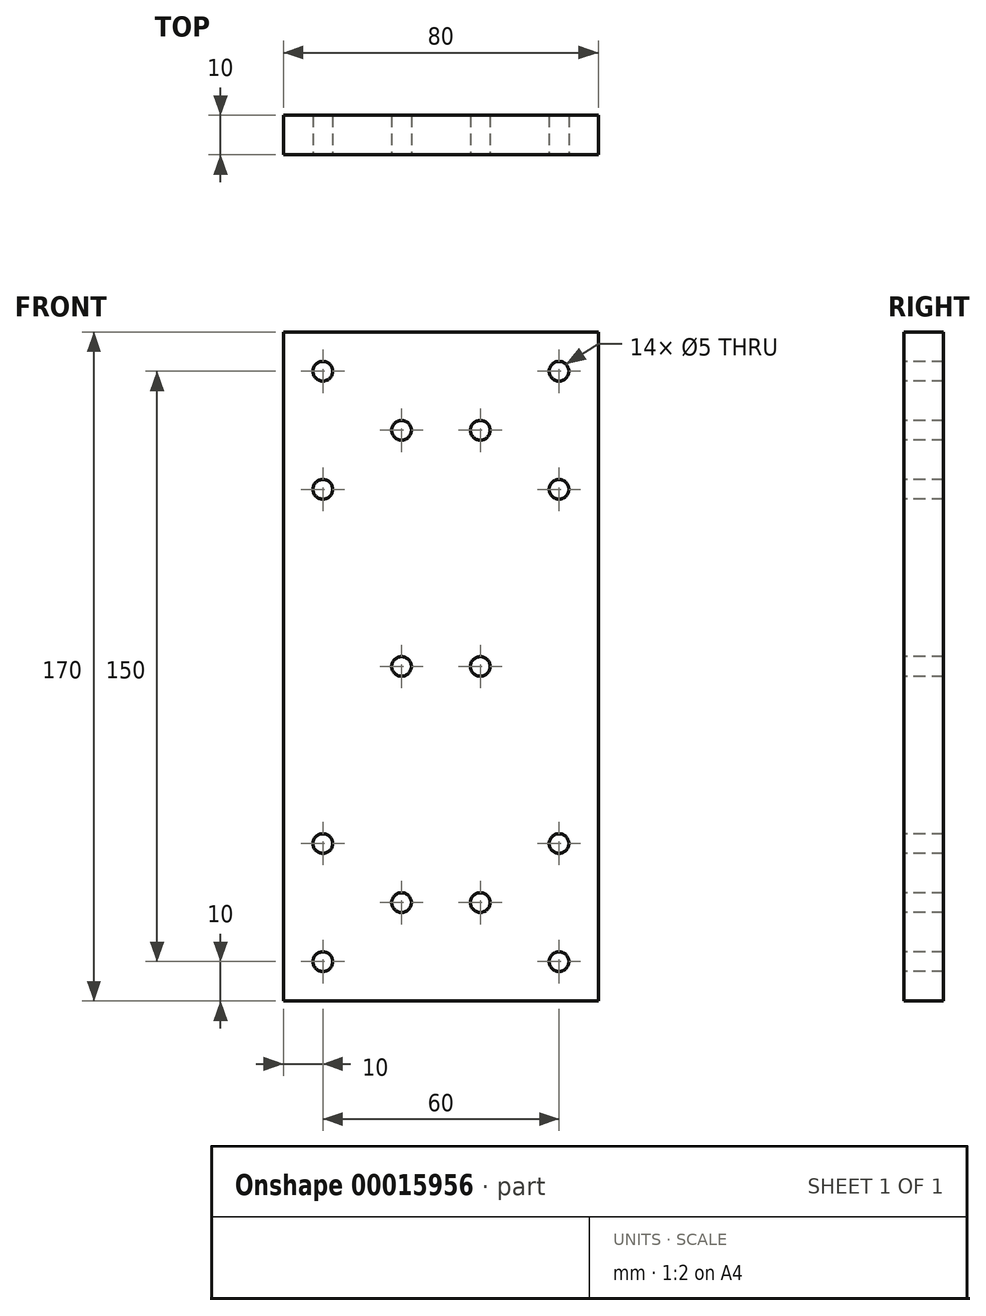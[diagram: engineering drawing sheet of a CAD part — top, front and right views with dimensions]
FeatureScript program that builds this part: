
annotation { "Feature Type Name" : "Feature", "Feature Type Description" : "" }
export const myFeature = defineFeature(function(context is Context, id is Id, definition is map)
    precondition{}
    {
        {
            var Q0;
            Q0=qCreatedBy(makeId("Front.planeOp"),FACE);
            var sketch = newSketch(context, id + "F0", { "sketchPlane" : qUnion([Q0])});
            skLineSegment(sketch, "E0.bottom", {"start": v(0, 0) * mm, "end": v(80, 0) * mm});
            skLineSegment(sketch, "E0.top", {"start": v(0, 170) * mm, "end": v(80, 170) * mm});
            skLineSegment(sketch, "E0.left", {"start": v(0, 0) * mm, "end": v(0, 170) * mm});
            skLineSegment(sketch, "E0.right", {"start": v(80, 0) * mm, "end": v(80, 170) * mm});
            skSolve(sketch);
        }
        {
            var Q0;
            Q0 = qSketchRegion(id + "F0", true);
            extrude(context, id + "F1", {"entities" : qUnion([Q0]), "oppositeDirection" : true, "depth" : 10 * mm});
        }
        {
            var Q0;
            Q0=makeQuery(id+"F1.opExtrude","CAP_FACE",FACE,{"disambiguationData":[OSD([sQuery(id+"F0.wireOp",EDGE,"E0.bottom"),sQuery(id+"F0.wireOp",EDGE,"E0.top"),sQuery(id+"F0.wireOp",EDGE,"E0.left"),sQuery(id+"F0.wireOp",EDGE,"E0.right")])],"isStart":true});
            var sketch = newSketch(context, id + "F2", { "sketchPlane" : qUnion([Q0])});
            skLineSegment(sketch, "E1.0", {"start": v(0, 160) * mm, "end": v(80, 160) * mm, "construction": true});
            skLineSegment(sketch, "E2.0", {"start": v(10, 0) * mm, "end": v(10, 170) * mm, "construction": true});
            skLineSegment(sketch, "E3.0", {"start": v(0, 10) * mm, "end": v(80, 10) * mm, "construction": true});
            skLineSegment(sketch, "E4", {"start": v(40, 170) * mm, "end": v(40, 0) * mm, "construction": true});
            skLineSegment(sketch, "E5", {"start": v(80, 85) * mm, "end": v(0, 85) * mm, "construction": true});
            skLineSegment(sketch, "E6.0", {"start": v(0, 130) * mm, "end": v(80, 130) * mm, "construction": true});
            skCircle(sketch, "E7", {"center": v(10, 160) * mm, "radius": 2.5 * mm});
            skCircle(sketch, "E8", {"center": v(10, 130) * mm, "radius": 2.5 * mm});
            skCircle(sketch, "E9.MirrorC", {"center": v(70, 160) * mm, "radius": 2.5 * mm});
            skCircle(sketch, "E10.MirrorC", {"center": v(70, 130) * mm, "radius": 2.5 * mm});
            skCircle(sketch, "E11.MirrorC", {"center": v(10, 40) * mm, "radius": 2.5 * mm});
            skCircle(sketch, "E12.MirrorC", {"center": v(10, 10) * mm, "radius": 2.5 * mm});
            skCircle(sketch, "E13.MirrorC", {"center": v(70, 10) * mm, "radius": 2.5 * mm});
            skCircle(sketch, "E14.MirrorC", {"center": v(70, 40) * mm, "radius": 2.5 * mm});
            skLineSegment(sketch, "E15.0", {"start": v(50, 170) * mm, "end": v(50, 0) * mm, "construction": true});
            skLineSegment(sketch, "E16.0", {"start": v(30, 170) * mm, "end": v(30, 0) * mm, "construction": true});
            skLineSegment(sketch, "E17.0", {"start": v(0, 145) * mm, "end": v(80, 145) * mm, "construction": true});
            skCircle(sketch, "E18", {"center": v(30, 145) * mm, "radius": 2.5 * mm});
            skCircle(sketch, "E19", {"center": v(30, 85) * mm, "radius": 2.5 * mm});
            skCircle(sketch, "E20.MirrorC", {"center": v(50, 145) * mm, "radius": 2.5 * mm});
            skCircle(sketch, "E21.MirrorC", {"center": v(50, 85) * mm, "radius": 2.5 * mm});
            skCircle(sketch, "E22.MirrorC", {"center": v(30, 25) * mm, "radius": 2.5 * mm});
            skCircle(sketch, "E23.MirrorC", {"center": v(50, 25) * mm, "radius": 2.5 * mm});
            skSolve(sketch);
        }
        {
            var Q0;
            Q0 = qSketchRegion(id + "F2", true);
            extrude(context, id + "F3", {"entities" : qUnion([Q0]), "operationType" : NewBodyOperationType.REMOVE, "endBound" : BoundingType.THROUGH_ALL, "oppositeDirection" : true, "depth" : 25 * mm});
        }
    });
